# Revit family: Stay_Floor_Mounted_
name_source: partatom
category: Casework
units: mm (PartAtom-declared; Revit-internal decimal feet)

## family parameters
Always vertical = Yes
Cut with Voids When Loaded = No
OmniClass Number = 23.40.35.00
OmniClass Title = Casework
Room Calculation Point = No
Shared = No
Work Plane-Based = No

## types (6) — shared parameters
Manufacturer = Väinö Korpinen Oy
URL = http://www.korpinen.com
zero-valued in all types: Depth, Height, Width

## per-type parameters (varying)
| type | Adjustable Height | Model | Type |
| Stay 10104 | No | 10104 - Stay 4 Floor Mounted | Stay : 10113 |
| Stay 10104 K | No | 10104 K - Stay 4 Floor Mounted | Stay : 10113 K |
| Stay 10104 P | No | 10104 P - Stay 4 Floor Mounted | Stay : 10113 P |
| Stay 10111 | Yes | 10111 - Stay 11 Floor Mounted | Stay : 10113 |
| Stay 10111 K | Yes | 10111 K - Stay 11 Floor Mounted | Stay : 10113 K |
| Stay 10111 P | Yes | 10111 K - Stay 11 Floor Mounted | Stay : 10113 P |

## geometry (parser evidence)
native form markers: Blend x4, Sweep x12
no freeform markers — native parametric forms only
